# Revit family: XFF-TEE
name_source: partatom
category: Conexões de tubo
units: mm (PartAtom-declared; Revit-internal decimal feet)

## family parameters
Com base no plano de trabalho = Não
Compartilhado = Não
Corte com vazios quando carregada = Não
Cota do conector redondo = Utilizar diâmetro
Sempre na vertical = Sim
Tipo de parte = Tê

## types (1)
- XFF-TEE
    DTT1 = 3  [stored 0.00984252 ft]
    DTT2 = 2  [stored 0.00656168 ft]
    DTT3 = 10  [stored 0.0328084 ft]
    DTT4 = 1  [stored 0.00328084 ft]
    DTT5 = 26
    Descrição = XFF-TEE: 17mm Barb x Barb x Barb Tee
    Elevação padrão = 0  [stored 0 ft]
    Modelo = XFF-TEE
    PVC = PVC - Franklin Electric - Preto
    RainBird: Description = XFF-TEE: 17mm Barb x Barb x Barb Tee
    RainBird: Product Link = www.rainbird.com
    SupportProjetos: Level of Detail = LOD 300
    SupportProjetos: Review = R00
    Tipo de imagem = <Nenhum>
    URL = www.rainbird.com
    Y2 = 43
    y = 9

note: [stored X ft] marks values corroborated as IEEE doubles in the binary element streams (Revit-internal decimal feet)

## geometry (parser evidence)
native form markers: Blend x4
no freeform markers — native parametric forms only
